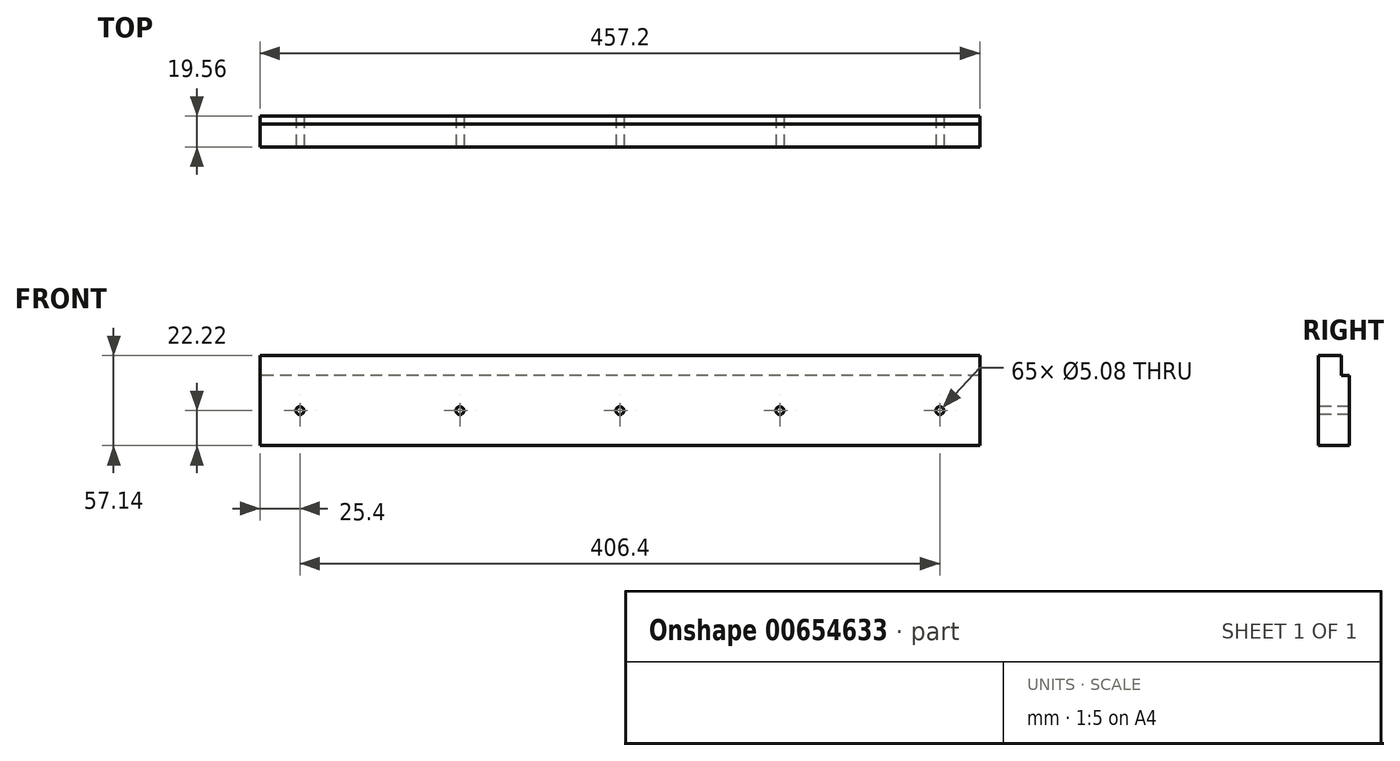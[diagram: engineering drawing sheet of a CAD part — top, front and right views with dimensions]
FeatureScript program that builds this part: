
annotation { "Feature Type Name" : "Feature", "Feature Type Description" : "" }
export const myFeature = defineFeature(function(context is Context, id is Id, definition is map)
    precondition{}
    {
        {
            var Q0;
            Q0=qCreatedBy(makeId("Front.planeOp"),FACE);
            var sketch = newSketch(context, id + "F0", { "sketchPlane" : qUnion([Q0])});
            skLineSegment(sketch, "E0.bottom", {"start": v(228.6, -28.57) * mm, "end": v(-228.6, -28.58) * mm});
            skLineSegment(sketch, "E0.top", {"start": v(228.6, 28.58) * mm, "end": v(-228.6, 28.57) * mm});
            skLineSegment(sketch, "E0.left", {"start": v(228.6, -28.57) * mm, "end": v(228.6, 28.58) * mm});
            skLineSegment(sketch, "E0.right", {"start": v(-228.6, -28.58) * mm, "end": v(-228.6, 28.57) * mm});
            skPoint(sketch, "E0.middle", {"position": v(0, 0) * mm});
            skSolve(sketch);
        }
        {
            var Q0;
            Q0 = qSketchRegion(id + "F0", true);
            extrude(context, id + "F1", {"entities" : qUnion([Q0]), "depth" : 19.56 * mm, "offsetDistance" : 25.4 * mm});
        }
        {
            var Q0;
            Q0=makeQuery(id+"F1.opExtrude","SWEPT_FACE",FACE,{"disambiguationData":[OSD([sQuery(id+"F0.wireOp",EDGE,"E0.right")])]});
            var sketch = newSketch(context, id + "F2", { "sketchPlane" : qUnion([Q0])});
            skLineSegment(sketch, "E1.bottom", {"start": v(0, 28.57) * mm, "end": v(5.08, 28.57) * mm});
            skLineSegment(sketch, "E1.top", {"start": v(0, 15.87) * mm, "end": v(5.08, 15.87) * mm});
            skLineSegment(sketch, "E1.left", {"start": v(0, 28.57) * mm, "end": v(0, 15.87) * mm});
            skLineSegment(sketch, "E1.right", {"start": v(5.08, 28.57) * mm, "end": v(5.08, 15.87) * mm});
            skPoint(sketch, "E2.firstSnap0", {"position": v(2.54, 28.57) * mm});
            skSolve(sketch);
        }
        {
            var Q0;
            Q0=makeQuery(id+"F2.imprint","IMPRINT",FACE,{"disambiguationData":[TD([[makeQuery(id+"F2.imprint","IMPRINT",EDGE,{"derivedFrom":sQuery(id+"F2.wireOp",EDGE,"E1.bottom")}),1.0]])]});
            extrude(context, id + "F3", {"entities" : qUnion([Q0]), "operationType" : NewBodyOperationType.REMOVE, "endBound" : BoundingType.UP_TO_NEXT, "oppositeDirection" : true, "depth" : 25.4 * mm, "offsetDistance" : 25.4 * mm});
        }
        {
            var Q0;
            Q0=makeQuery(id+"F1.opExtrude","CAP_FACE",FACE,{"disambiguationData":[OSD([sQuery(id+"F0.wireOp",EDGE,"E0.bottom"),sQuery(id+"F0.wireOp",EDGE,"E0.top"),sQuery(id+"F0.wireOp",EDGE,"E0.left"),sQuery(id+"F0.wireOp",EDGE,"E0.right")])],"isStart":false});
            var sketch = newSketch(context, id + "F4", { "sketchPlane" : qUnion([Q0])});
            skLineSegment(sketch, "E3", {"start": v(0, -28.58) * mm, "end": v(0, -6.35) * mm});
            skLineSegment(sketch, "E4", {"start": v(0, -6.35) * mm, "end": v(-101.6, -6.35) * mm});
            skLineSegment(sketch, "E5", {"start": v(-101.6, -6.35) * mm, "end": v(-203.2, -6.35) * mm});
            skLineSegment(sketch, "E6", {"start": v(0, -6.35) * mm, "end": v(101.6, -6.35) * mm});
            skLineSegment(sketch, "E7", {"start": v(101.6, -6.35) * mm, "end": v(203.2, -6.35) * mm});
            skCircle(sketch, "E8", {"center": v(-203.2, -6.35) * mm, "radius": 2.54 * mm});
            skCircle(sketch, "E9", {"center": v(-101.6, -6.35) * mm, "radius": 2.54 * mm});
            skCircle(sketch, "E10", {"center": v(0, -6.35) * mm, "radius": 2.54 * mm});
            skCircle(sketch, "E11", {"center": v(101.6, -6.35) * mm, "radius": 2.54 * mm});
            skCircle(sketch, "E12", {"center": v(203.2, -6.35) * mm, "radius": 2.54 * mm});
            skSolve(sketch);
        }
        {
            var Q0;
            Q0 = qSketchRegion(id + "F4", true);
            extrude(context, id + "F5", {"entities" : qUnion([Q0]), "operationType" : NewBodyOperationType.REMOVE, "endBound" : BoundingType.UP_TO_NEXT, "oppositeDirection" : true, "depth" : 25.4 * mm, "offsetDistance" : 25.4 * mm});
        }
    });
